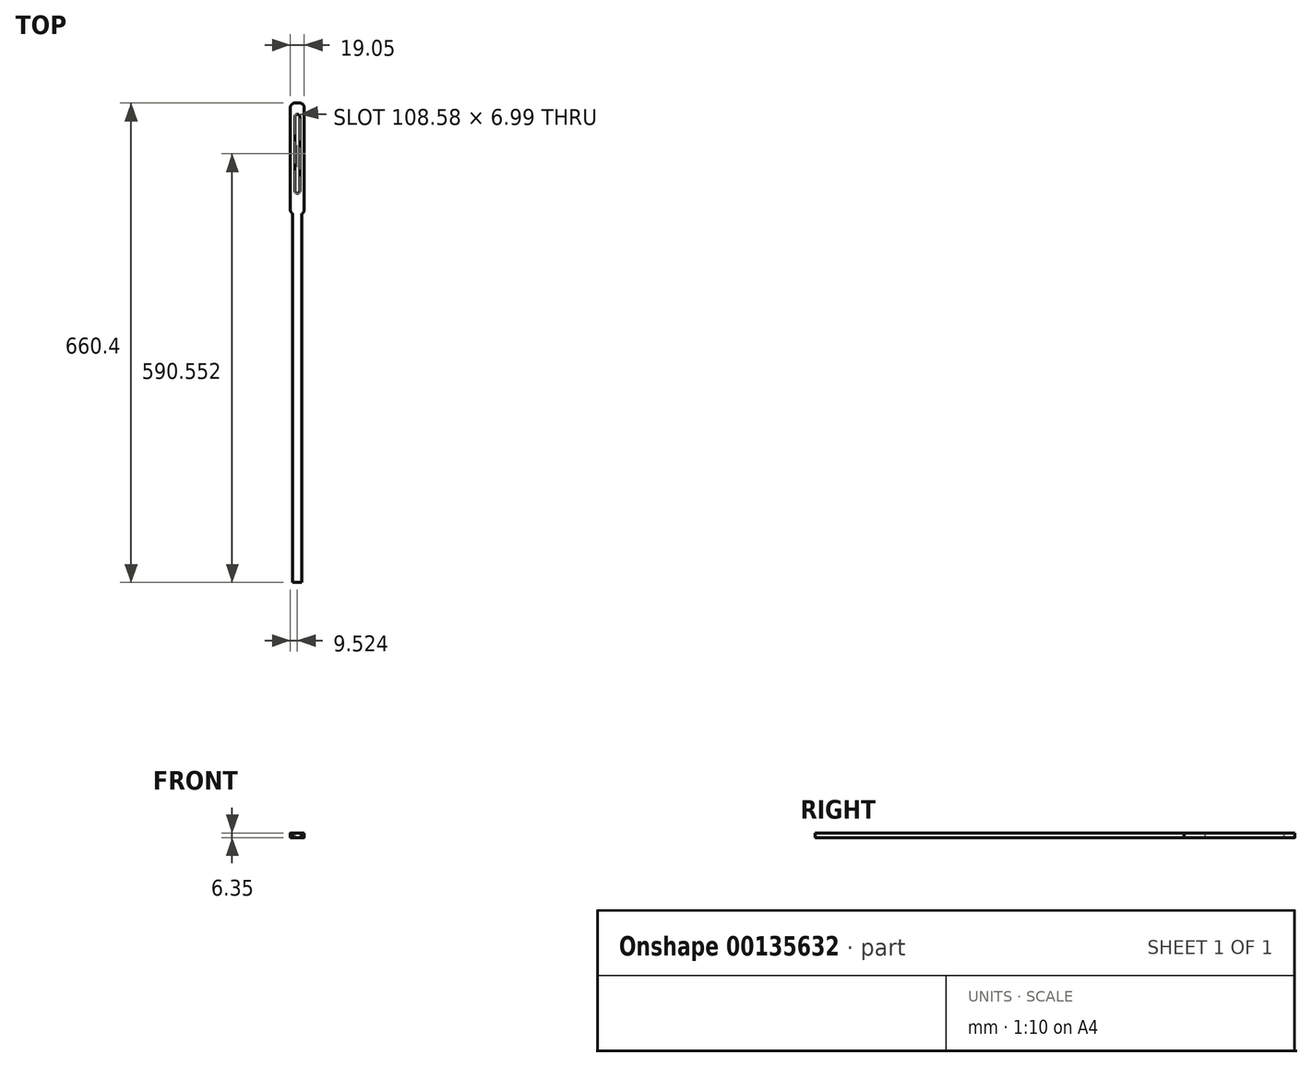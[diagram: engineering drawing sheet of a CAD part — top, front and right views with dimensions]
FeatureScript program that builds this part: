
annotation { "Feature Type Name" : "Feature", "Feature Type Description" : "" }
export const myFeature = defineFeature(function(context is Context, id is Id, definition is map)
    precondition{}
    {
        {
            var Q0;
            Q0=qCreatedBy(makeId("Top.planeOp"),FACE);
            var sketch = newSketch(context, id + "F0", { "sketchPlane" : qUnion([Q0])});
            skLineSegment(sketch, "E0.bottom", {"start": v(-22.2, 592.27) * mm, "end": v(-3.15, 592.27) * mm});
            skLineSegment(sketch, "E0.top", {"start": v(-22.2, 439.87) * mm, "end": v(-19.03, 439.87) * mm});
            skLineSegment(sketch, "E0.left", {"start": v(-22.2, 592.27) * mm, "end": v(-22.2, 439.87) * mm});
            skLineSegment(sketch, "E0.right", {"start": v(-3.15, 592.27) * mm, "end": v(-3.15, 439.87) * mm});
            skLineSegment(sketch, "E1.top", {"start": v(-19.03, -68.13) * mm, "end": v(-6.33, -68.13) * mm});
            skLineSegment(sketch, "E1.left", {"start": v(-19.03, 439.87) * mm, "end": v(-19.03, -68.13) * mm});
            skLineSegment(sketch, "E1.right", {"start": v(-6.33, 439.87) * mm, "end": v(-6.33, -68.13) * mm});
            skLineSegment(sketch, "E2.trimOffspring", {"start": v(-6.33, 439.87) * mm, "end": v(-3.15, 439.87) * mm});
            skLineSegment(sketch, "E3", {"start": v(-12.68, 592.27) * mm, "end": v(-12.68, -68.13) * mm, "construction": true});
            skSolve(sketch);
        }
        {
            var Q0;
            Q0=makeQuery(id+"F0.imprint","IMPRINT",FACE,{"disambiguationData":[TD([[makeQuery(id+"F0.imprint","IMPRINT",EDGE,{"derivedFrom":sQuery(id+"F0.wireOp",EDGE,"E0.bottom")}),-1.0]])]});
            extrude(context, id + "F1", {"entities" : qUnion([Q0]), "depth" : 6.35 * mm});
        }
        {
            var Q0;
            Q0=makeQuery(id+"F1.opExtrude","SWEPT_EDGE",EDGE,{"disambiguationData":[OSD([sQuery(id+"F0.wireOp",EDGE,"E0.bottom"),sQuery(id+"F0.wireOp",EDGE,"E0.right")])]});
            var Q1;
            Q1=makeQuery(id+"F1.opExtrude","SWEPT_EDGE",EDGE,{"disambiguationData":[OSD([sQuery(id+"F0.wireOp",EDGE,"E0.bottom"),sQuery(id+"F0.wireOp",EDGE,"E0.left")])]});
            var Q2;
            Q2=makeQuery(id+"F1.opExtrude","SWEPT_EDGE",EDGE,{"disambiguationData":[OSD([sQuery(id+"F0.wireOp",EDGE,"E0.top"),sQuery(id+"F0.wireOp",EDGE,"E0.left")])]});
            var Q3;
            Q3=makeQuery(id+"F1.opExtrude","SWEPT_EDGE",EDGE,{"disambiguationData":[OSD([sQuery(id+"F0.wireOp",EDGE,"E0.right"),sQuery(id+"F0.wireOp",EDGE,"E2.trimOffspring")])]});
            fillet(context, id + "F2", {"entities" : qUnion([Q0, Q1, Q2, Q3]), "radius" : 6.35 * mm, "tangentPropagation" : true, "allowEdgeOverflow" : false});
        }
        {
            var Q0;
            Q0=makeQuery(id+"F1.opExtrude","CAP_FACE",FACE,{"disambiguationData":[OSD([sQuery(id+"F0.wireOp",EDGE,"E0.bottom"),sQuery(id+"F0.wireOp",EDGE,"E0.top"),sQuery(id+"F0.wireOp",EDGE,"E0.left"),sQuery(id+"F0.wireOp",EDGE,"E0.right"),sQuery(id+"F0.wireOp",EDGE,"E1.top"),sQuery(id+"F0.wireOp",EDGE,"E1.left"),sQuery(id+"F0.wireOp",EDGE,"E1.right"),sQuery(id+"F0.wireOp",EDGE,"E2.trimOffspring")])],"isStart":true});
            var sketch = newSketch(context, id + "F3", { "sketchPlane" : qUnion([Q0])});
            skArc(sketch, "E4", {"start": v(-16.17, -573.22) * mm, "mid": v(-12.68, -576.71) * mm, "end": v(-9.18, -573.22) * mm});
            skPoint(sketch, "E4.centerSnap0", {"position": v(-12.68, -592.27) * mm});
            skArc(sketch, "E5", {"start": v(-9.18, -471.62) * mm, "mid": v(-12.68, -468.13) * mm, "end": v(-16.17, -471.62) * mm});
            skLineSegment(sketch, "E6", {"start": v(-12.68, -592.27) * mm, "end": v(-12.68, -573.22) * mm, "construction": true});
            skLineSegment(sketch, "E7", {"start": v(-9.18, -573.35) * mm, "end": v(-9.18, -471.62) * mm});
            skLineSegment(sketch, "E8", {"start": v(-16.17, -471.62) * mm, "end": v(-16.17, -573.22) * mm});
            skSolve(sketch);
        }
        {
            var Q0;
            {var subQ0=sQuery(id+"F3.wireOp",EDGE,"E4");Q0=makeQuery(id+"F3.imprint","IMPRINT",FACE,{"disambiguationData":[TD([[makeQuery(id+"F3.imprint","IMPRINT",EDGE,{"derivedFrom":subQ0}),1.0]])]});}
            extrude(context, id + "F4", {"entities" : qUnion([Q0]), "operationType" : NewBodyOperationType.REMOVE, "endBound" : BoundingType.THROUGH_ALL, "oppositeDirection" : true, "depth" : 25.4 * mm});
        }
    });
